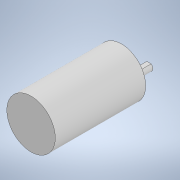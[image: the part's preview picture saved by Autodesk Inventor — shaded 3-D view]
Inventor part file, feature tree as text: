
AUTODESK INVENTOR PART (.ipt)
format: ipt  version: 2020.2 (Build 242310000, 310)  size: 136,192 bytes
history: native  units: mm
features: extrude x4, sketch x4, hole x1
ambient origin geometry x8: Origin, YZ Plane, XZ Plane, XY Plane, X Axis, Y Axis, Z Axis, Center Point
bodies: Solido1 (feature_tree)
feature tree (9):
  extrude  "Estrusione1"  Depth=37.0mm
  hole  "Foro1"  [1 undecoded]
  extrude  "Estrusione2"  Depth=15.3mm
  extrude  "Estrusione3"  TaperAngle=0.0deg  [1 undecoded]
  extrude  "Estrusione4"  Depth=60.0mm TaperAngle=360.0deg
  sketch  "Schizzo1"
  sketch  "Schizzo2"
  sketch  "Schizzo4"
  sketch  "Schizzo5"
note: 2 required parameter values undecoded (feature->parameter linkage not recoverable at this tier; creation-order binding heuristic only, values carry confidence <= 0.55)
